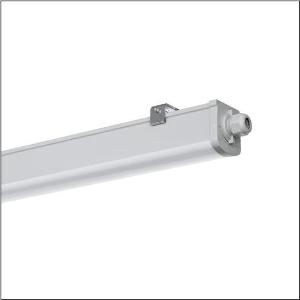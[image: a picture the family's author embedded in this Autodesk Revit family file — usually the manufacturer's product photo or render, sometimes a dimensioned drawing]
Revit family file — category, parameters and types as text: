
# Revit family: monsun_r__31_51fa207p460b_ddf4
name_source: partatom
category: Lighting Fixtures
units: mm (PartAtom-declared; Revit-internal decimal feet)

## family parameters
Cut with Voids When Loaded = No
Host = Face
Light Source = No
Part Type = Normal
Room Calculation Point = No
Round Connector Dimension = Use Diameter
Shared = No

## types (1)
- Monsun® 31 (1 x LED, 6700 lm, 50 W, 4000K)
    Apparent Load = 50 VA
    CIE Flux Codes = 42 72 91 92 100
    Color Rendering = 80
    Color Temperature = 4000K
    Default Elevation = 1800 mm
    Description = Monsun® 31, damp-proof luminaire, primary optical cover: diffuser, of PC, frosted, light emission: direct distribution, primary light characteristic: symmetric, installation type: surface-mounted, LED, rated luminous flux: 6.700lm, luminous efficacy: 134lm/W, light colour: 840, colour temperature: 4000K, control gear: ECG, with terminal, 3+1-pole, max. 2.5mm², through-wiring: 3x 2.5mm² + 1x 1.5mm², mains connection: 220..240V, AC, 50/60Hz, rated input power: 50W, housing, luminaire housing, of PC, light grey (RAL 7035), length: 1.458mm, width: 68mm, height: 76mm, protection rating (complete): IP66, insulation class (complete): insulation class II (safety insulation), certification: CE, ENEC, UKCA, protection symbol: D, impact resistance: IK08, permissible operating ambient temperature: -20..+40°C, corresponds to IFS (International Featured Standards) requirements for safety and quality in the food industry, contact your sales advisor before using the luminaires in applications with unclear chemical exposure, large temperature fluctuations or condensation-forming humidity, packaging unit: 1 piece
    Height = 77 mm
    Lamp = 1 x LED
    Lamp Light Flux = 6700 lm
    Lamp Power = 50 W
    Lamp count = 1
    Length = 1518 mm
    Luminous efficacy = 134 lm/W
    Manufacturer = Siteco
    ModVariant = No
    Model = 51FA207P460B
    Mounting Place = Ceiling
    Mounting Type = Surface mounted
    Number of Poles = 1
    OnlyDefault = Yes
    Power Factor = 1
    Product Name = Monsun® 31
    Product group = damp-proof luminaire
    ProductGroupID = 300
    Protection Class = Protection class II
    Protection Degree = IP 66
    RLX_Detail_Level = 1
    RLX_Emergency_Light_Flux = 0 lm
    RLX_Emergency_Type = 0
    RLX_Emergency_Type_DB = No
    RlxData = <blob elided: 33265 chars, md5=ad1c1cf5>
    Socket = socket
    Standby Power = 0 W
    System Light Flux = 6700 lm
    System Power = 50 W
    Type Comments = Product without accessories
    Type Image = l_1006174.jpg
    URL = http://relux.com
    VarID = ---
    Voltage = 0 V
    Weight = 0.00 kg
    Width = 69 mm

## geometry (parser evidence)
native form markers: Blend x4, Sweep x14
no freeform markers — native parametric forms only
